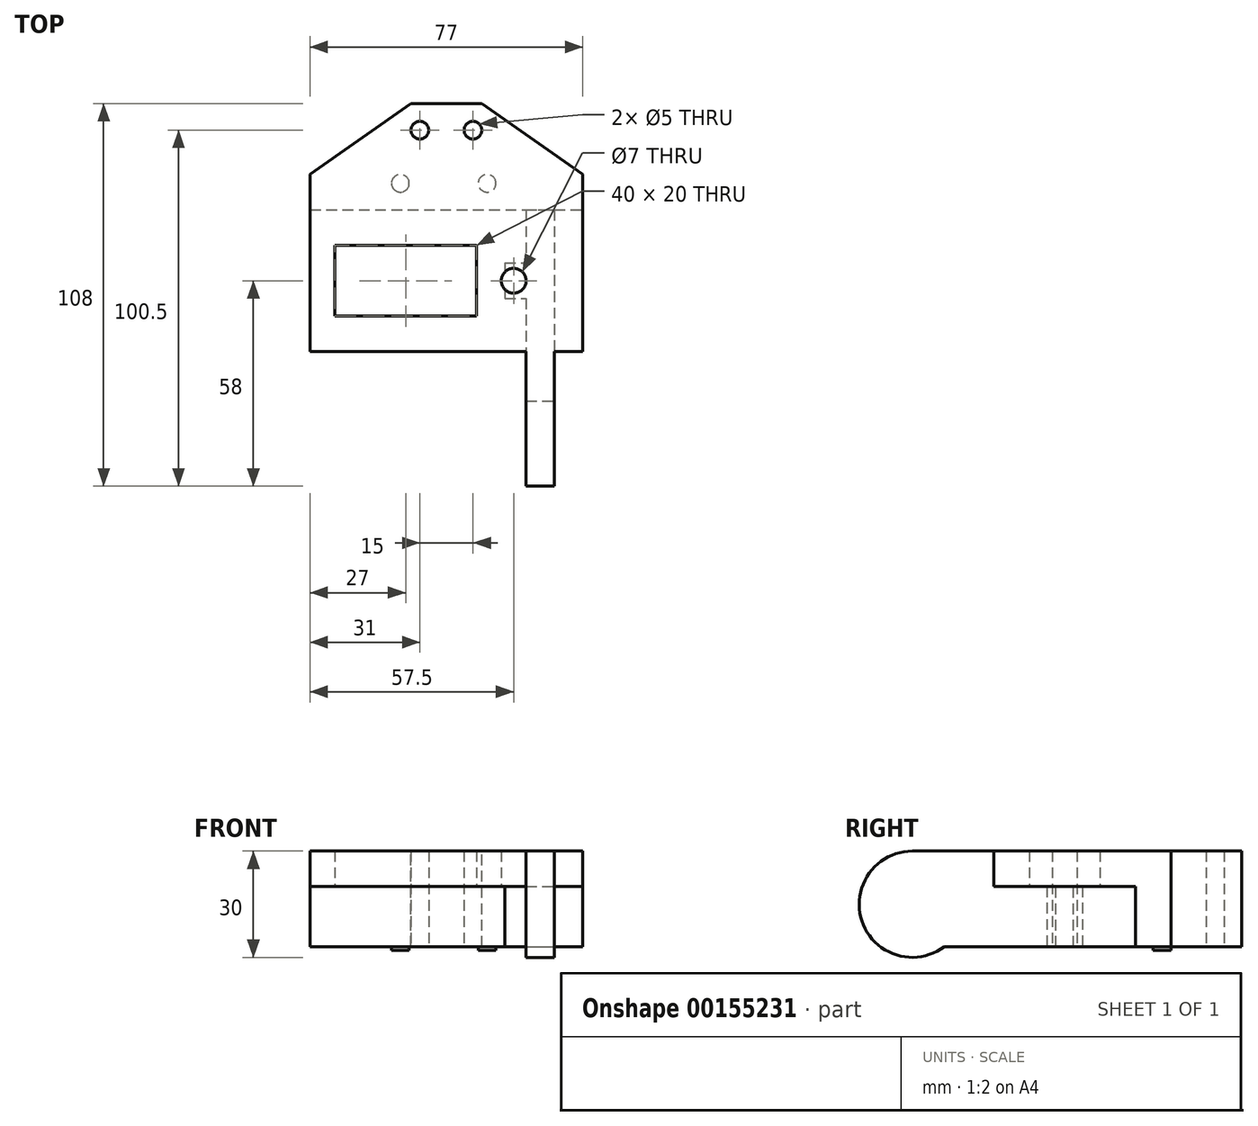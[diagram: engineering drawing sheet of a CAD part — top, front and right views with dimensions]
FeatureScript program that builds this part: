
annotation { "Feature Type Name" : "Feature", "Feature Type Description" : "" }
export const myFeature = defineFeature(function(context is Context, id is Id, definition is map)
    precondition{}
    {
        {
            var Q0;
            Q0=qCreatedBy(makeId("Top.planeOp"),FACE);
            var sketch = newSketch(context, id + "F0", { "sketchPlane" : qUnion([Q0])});
            skLineSegment(sketch, "E0.bottom", {"start": v(-38.5, 20) * mm, "end": v(38.5, 20) * mm});
            skLineSegment(sketch, "E0.top", {"start": v(-38.5, -20) * mm, "end": v(38.5, -20) * mm});
            skLineSegment(sketch, "E0.left", {"start": v(-38.5, 20) * mm, "end": v(-38.5, -20) * mm});
            skLineSegment(sketch, "E0.right", {"start": v(38.5, 20) * mm, "end": v(38.5, -20) * mm});
            skLineSegment(sketch, "E1.bottom", {"start": v(-31.5, 10) * mm, "end": v(8.5, 10) * mm});
            skLineSegment(sketch, "E1.top", {"start": v(-31.5, -10) * mm, "end": v(8.5, -10) * mm});
            skLineSegment(sketch, "E1.left", {"start": v(-31.5, 10) * mm, "end": v(-31.5, -10) * mm});
            skLineSegment(sketch, "E1.right", {"start": v(8.5, 10) * mm, "end": v(8.5, -10) * mm});
            skCircle(sketch, "E2", {"center": v(19, 0) * mm, "radius": 3.5 * mm});
            skPoint(sketch, "E2.centerSnap0", {"position": v(-31.5, 0) * mm});
            skSolve(sketch);
        }
        {
            var Q0;
            Q0 = qSketchRegion(id + "F0", true);
            extrude(context, id + "F1", {"entities" : qUnion([Q0]), "depth" : 10 * mm});
        }
        {
            var Q0;
            Q0=makeQuery(id+"F1.opExtrude","CAP_FACE",FACE,{"disambiguationData":[OSD([sQuery(id+"F0.wireOp",EDGE,"E0.bottom"),sQuery(id+"F0.wireOp",EDGE,"E0.top"),sQuery(id+"F0.wireOp",EDGE,"E0.left"),sQuery(id+"F0.wireOp",EDGE,"E0.right"),sQuery(id+"F0.wireOp",EDGE,"E1.bottom"),sQuery(id+"F0.wireOp",EDGE,"E1.top"),sQuery(id+"F0.wireOp",EDGE,"E1.left"),sQuery(id+"F0.wireOp",EDGE,"E1.right")])],"isStart":false});
            var sketch = newSketch(context, id + "F2", { "sketchPlane" : qUnion([Q0])});
            skLineSegment(sketch, "E3.bottom", {"start": v(-38.5, 20) * mm, "end": v(38.5, 20) * mm});
            skLineSegment(sketch, "E3.top", {"start": v(-38.5, 30) * mm, "end": v(38.5, 30) * mm});
            skLineSegment(sketch, "E3.left", {"start": v(-38.5, 20) * mm, "end": v(-38.5, 30) * mm});
            skLineSegment(sketch, "E3.right", {"start": v(38.5, 20) * mm, "end": v(38.5, 30) * mm});
            skLineSegment(sketch, "E4.bottom", {"start": v(-10, 30) * mm, "end": v(10, 30) * mm});
            skLineSegment(sketch, "E4.top", {"start": v(-10, 50) * mm, "end": v(10, 50) * mm});
            skLineSegment(sketch, "E4.left", {"start": v(-10, 30) * mm, "end": v(-10, 50) * mm});
            skLineSegment(sketch, "E4.right", {"start": v(10, 30) * mm, "end": v(10, 50) * mm});
            skLineSegment(sketch, "E5", {"start": v(-38.5, 30) * mm, "end": v(-10, 50) * mm});
            skLineSegment(sketch, "E6", {"start": v(10, 50) * mm, "end": v(38.5, 30) * mm});
            skSolve(sketch);
        }
        {
            var Q0;
            Q0 = qSketchRegion(id + "F2", true);
            extrude(context, id + "F3", {"entities" : qUnion([Q0]), "operationType" : NewBodyOperationType.ADD, "oppositeDirection" : true, "depth" : 27 * mm});
        }
        {
            var Q0;
            Q0=makeQuery(id+"F3.opExtrude","CAP_FACE",FACE,{"disambiguationData":[OSD([sQuery(id+"F2.wireOp",EDGE,"E3.bottom"),sQuery(id+"F2.wireOp",EDGE,"E3.left"),sQuery(id+"F2.wireOp",EDGE,"E3.right"),sQuery(id+"F2.wireOp",EDGE,"E4.top"),sQuery(id+"F2.wireOp",EDGE,"E5"),sQuery(id+"F2.wireOp",EDGE,"E6")])],"isStart":false});
            var sketch = newSketch(context, id + "F4", { "sketchPlane" : qUnion([Q0])});
            skCircle(sketch, "E7", {"center": v(-7.5, -42.5) * mm, "radius": 2.5 * mm});
            skCircle(sketch, "E8", {"center": v(7.5, -42.5) * mm, "radius": 2.5 * mm});
            skSolve(sketch);
        }
        {
            var Q0;
            Q0 = qSketchRegion(id + "F4", true);
            extrude(context, id + "F5", {"entities" : qUnion([Q0]), "operationType" : NewBodyOperationType.REMOVE, "oppositeDirection" : true, "depth" : 127 * mm});
        }
        {
            var Q0;
            Q0=makeQuery(id+"F1.opExtrude","SWEPT_FACE",FACE,{"disambiguationData":[OSD([sQuery(id+"F0.wireOp",EDGE,"E0.top")])]});
            var sketch = newSketch(context, id + "F6", { "sketchPlane" : qUnion([Q0])});
            skSolve(sketch);
        }
        {
            var Q0;
            {var subQ0=sQuery(id+"F0.wireOp",EDGE,"E0.top");Q0=makeQuery(id+"F6.imprint","IMPRINT",FACE,{"disambiguationData":[TD([[makeQuery(id+"F6.imprint","IMPRINT",EDGE,{"derivedFrom":makeQuery(id+"F1.opExtrude","CAP_EDGE",EDGE,{"disambiguationData":[OSD([subQ0])],"isStart":true})}),1.0]])]});}
            var sketch = newSketch(context, id + "F7", { "sketchPlane" : qUnion([Q0])});
            skLineSegment(sketch, "E9.top", {"start": v(22.5, -20) * mm, "end": v(30.5, -20) * mm});
            skLineSegment(sketch, "E9.left", {"start": v(22.5, 10) * mm, "end": v(22.5, -20) * mm});
            skLineSegment(sketch, "E10", {"start": v(30.5, -20) * mm, "end": v(30.5, 10) * mm});
            skLineSegment(sketch, "E11", {"start": v(30.5, 10) * mm, "end": v(22.5, 10) * mm});
            skLineSegment(sketch, "E12", {"start": v(22.5, 10) * mm, "end": v(22.5, 10) * mm});
            skSolve(sketch);
        }
        {
            var Q0;
            Q0 = qSketchRegion(id + "F7", true);
            extrude(context, id + "F8", {"entities" : qUnion([Q0]), "operationType" : NewBodyOperationType.ADD, "depth" : 38 * mm});
        }
        {
            var Q0;
            Q0=makeQuery(id+"F1HjtU2zzoWoDq2_1.boolean.opBoolean","MERGE",FACE,{"derivedFrom":[makeQuery(id+"F8.opExtrude","SWEPT_FACE",FACE,{"disambiguationData":[OSD([sQuery(id+"F7.wireOp",EDGE,"E9.left")])]}),makeQuery(id+"F1HjtU2zzoWoDq2_1.opExtrude","CAP_FACE",FACE,{"disambiguationData":[OSD([sQuery(id+"Fqk1zAMo2bsuies_1.wireOp",EDGE,"MgKvwTRx-y31f-WZWc-Caib-XEiZ7ANXJcK6.top"),sQuery(id+"Fqk1zAMo2bsuies_1.wireOp",EDGE,"MgKvwTRx-y31f-WZWc-Caib-XEiZ7ANXJcK6.left"),sQuery(id+"Fqk1zAMo2bsuies_1.wireOp",EDGE,"IRrUIqiS-T0Xg-A9l2-gfDi-nQQcYmAuvp0d"),sQuery(id+"Fqk1zAMo2bsuies_1.wireOp",EDGE,"oe0BP48I-Ls7v-YU94-uGDd-tbWBrKYAtibt")])],"isStart":true})]});
            var sketch = newSketch(context, id + "F9", { "sketchPlane" : qUnion([Q0])});
            skArc(sketch, "E13", {"start": v(43, -20) * mm, "mid": v(58, -5) * mm, "end": v(43, 10) * mm});
            skLineSegment(sketch, "E14.bottom", {"start": v(43, 10) * mm, "end": v(58, 10) * mm});
            skLineSegment(sketch, "E14.top", {"start": v(43, -20) * mm, "end": v(58, -20) * mm});
            skLineSegment(sketch, "E14.right", {"start": v(58, 10) * mm, "end": v(58, -20) * mm});
            skSolve(sketch);
        }
        {
            var Q0;
            Q0 = qSketchRegion(id + "F9", true);
            extrude(context, id + "F10", {"entities" : qUnion([Q0]), "operationType" : NewBodyOperationType.REMOVE, "oppositeDirection" : true, "depth" : 25.4 * mm});
        }
        {
            var Q0;
            Q0=makeQuery(id+"F8.opExtrude","SWEPT_FACE",FACE,{"disambiguationData":[OSD([sQuery(id+"F7.wireOp",EDGE,"E10")])]});
            var sketch = newSketch(context, id + "F11", { "sketchPlane" : qUnion([Q0])});
            skLineSegment(sketch, "E15", {"start": v(19.98, -17) * mm, "end": v(19.98, 0) * mm});
            skLineSegment(sketch, "E16", {"start": v(19.98, 0) * mm, "end": v(-20, 0) * mm});
            skLineSegment(sketch, "E17", {"start": v(-20, 0) * mm, "end": v(-20, -20) * mm});
            skLineSegment(sketch, "E18", {"start": v(19.98, -17) * mm, "end": v(-20, -17) * mm});
            skSolve(sketch);
        }
        {
            var Q0;
            Q0 = qSketchRegion(id + "F11", true);
            extrude(context, id + "F12", {"entities" : qUnion([Q0]), "operationType" : NewBodyOperationType.ADD, "oppositeDirection" : true, "depth" : 8 * mm});
        }
        {
            var Q0;
            Q0=makeQuery(id+"F1.opExtrude","CAP_FACE",FACE,{"disambiguationData":[OSD([sQuery(id+"F0.wireOp",EDGE,"E0.bottom"),sQuery(id+"F0.wireOp",EDGE,"E0.top"),sQuery(id+"F0.wireOp",EDGE,"E0.left"),sQuery(id+"F0.wireOp",EDGE,"E0.right"),sQuery(id+"F0.wireOp",EDGE,"E1.bottom"),sQuery(id+"F0.wireOp",EDGE,"E1.top"),sQuery(id+"F0.wireOp",EDGE,"E1.left"),sQuery(id+"F0.wireOp",EDGE,"E1.right"),sQuery(id+"F0.wireOp",EDGE,"E2")])],"isStart":true});
            var sketch = newSketch(context, id + "F13", { "sketchPlane" : qUnion([Q0])});
            skCircle(sketch, "E19", {"center": v(19, 0) * mm, "radius": 3.5 * mm});
            skSolve(sketch);
        }
        {
            var Q0;
            Q0=makeQuery(id+"F12.boolean.opBoolean","MERGE",FACE,{"derivedFrom":[makeQuery(id+"F8.opExtrude","SWEPT_FACE",FACE,{"disambiguationData":[OSD([sQuery(id+"F7.wireOp",EDGE,"E9.left")])]}),makeQuery(id+"F12.opExtrude","CAP_FACE",FACE,{"disambiguationData":[OSD([sQuery(id+"F11.wireOp",EDGE,"E15"),sQuery(id+"F11.wireOp",EDGE,"E16"),sQuery(id+"F11.wireOp",EDGE,"E17"),sQuery(id+"F11.wireOp",EDGE,"E18")])],"isStart":false})]});
            var sketch = newSketch(context, id + "F14", { "sketchPlane" : qUnion([Q0])});
            skLineSegment(sketch, "E20.bottom", {"start": v(5, 0) * mm, "end": v(-5, 0) * mm});
            skLineSegment(sketch, "E20.top", {"start": v(5, -17) * mm, "end": v(-5, -17) * mm});
            skLineSegment(sketch, "E20.left", {"start": v(5, 0) * mm, "end": v(5, -17) * mm});
            skLineSegment(sketch, "E20.right", {"start": v(-5, 0) * mm, "end": v(-5, -17) * mm});
            skSolve(sketch);
        }
        {
            var Q0;
            Q0 = qSketchRegion(id + "F14", true);
            extrude(context, id + "F15", {"entities" : qUnion([Q0]), "operationType" : NewBodyOperationType.ADD, "depth" : 6 * mm});
        }
        {
            var Q0;
            Q0 = qSketchRegion(id + "F13", true);
            extrude(context, id + "F16", {"entities" : qUnion([Q0]), "operationType" : NewBodyOperationType.REMOVE, "depth" : 25.4 * mm});
        }
        {
            var Q0;
            Q0=makeQuery(id+"F12.boolean.opBoolean","MERGE",FACE,{"derivedFrom":[makeQuery(id+"F8.opExtrude","SWEPT_FACE",FACE,{"disambiguationData":[OSD([sQuery(id+"F7.wireOp",EDGE,"E10")])]}),makeQuery(id+"F12.opExtrude","CAP_FACE",FACE,{"disambiguationData":[OSD([sQuery(id+"F11.wireOp",EDGE,"E15"),sQuery(id+"F11.wireOp",EDGE,"E16"),sQuery(id+"F11.wireOp",EDGE,"E17"),sQuery(id+"F11.wireOp",EDGE,"E18")])],"isStart":true})]});
            var sketch = newSketch(context, id + "F17", { "sketchPlane" : qUnion([Q0])});
            skArc(sketch, "E21", {"start": v(-43, -20) * mm, "mid": v(-38.26, -19.23) * mm, "end": v(-34, -17) * mm});
            skLineSegment(sketch, "E22", {"start": v(-20, -17) * mm, "end": v(-34, -17) * mm});
            skLineSegment(sketch, "E23", {"start": v(-43, -20) * mm, "end": v(-20, -20) * mm});
            skLineSegment(sketch, "E24", {"start": v(-20, -20) * mm, "end": v(-20, -17) * mm});
            skSolve(sketch);
        }
        {
            var Q0;
            Q0 = qSketchRegion(id + "F17", true);
            extrude(context, id + "F18", {"entities" : qUnion([Q0]), "operationType" : NewBodyOperationType.REMOVE, "oppositeDirection" : true, "depth" : 25.4 * mm});
        }
        {
            var Q0;
            Q0=makeQuery(id+"F3.opExtrude","CAP_FACE",FACE,{"disambiguationData":[OSD([sQuery(id+"F2.wireOp",EDGE,"E3.bottom"),sQuery(id+"F2.wireOp",EDGE,"E3.left"),sQuery(id+"F2.wireOp",EDGE,"E3.right"),sQuery(id+"F2.wireOp",EDGE,"E4.top"),sQuery(id+"F2.wireOp",EDGE,"E5"),sQuery(id+"F2.wireOp",EDGE,"E6")])],"isStart":false});
            var sketch = newSketch(context, id + "F19", { "sketchPlane" : qUnion([Q0])});
            skCircle(sketch, "E25", {"center": v(11.5, -27.5) * mm, "radius": 2.5 * mm});
            skCircle(sketch, "E26", {"center": v(-13, -27.5) * mm, "radius": 2.5 * mm});
            skPoint(sketch, "E27.endSnap0", {"position": v(-38.5, -25) * mm});
            skSolve(sketch);
        }
        {
            var Q0;
            Q0 = qSketchRegion(id + "F19", true);
            extrude(context, id + "F20", {"entities" : qUnion([Q0]), "operationType" : NewBodyOperationType.ADD, "depth" : 1 * mm});
        }
    });
